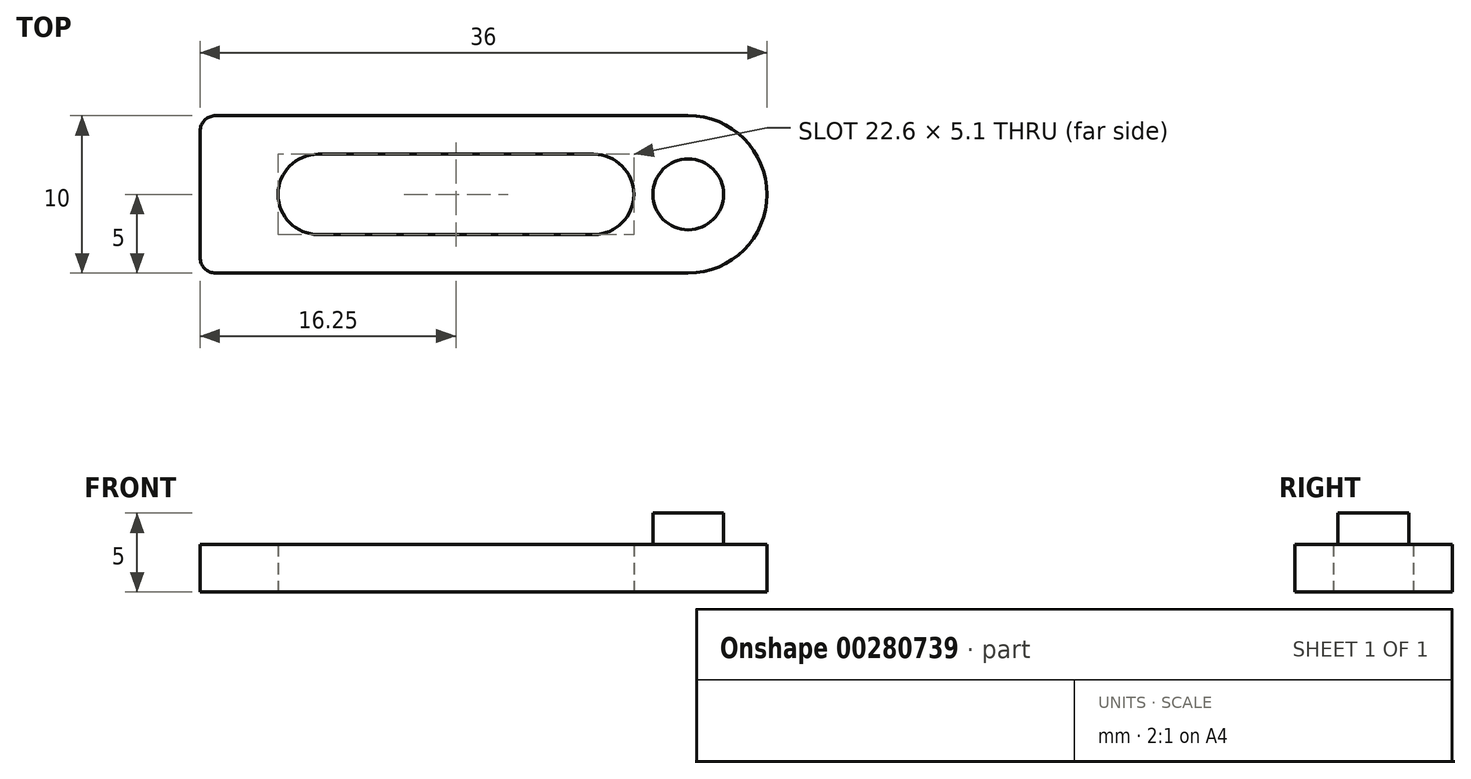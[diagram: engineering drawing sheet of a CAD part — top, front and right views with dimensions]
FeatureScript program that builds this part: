
annotation { "Feature Type Name" : "Feature", "Feature Type Description" : "" }
export const myFeature = defineFeature(function(context is Context, id is Id, definition is map)
    precondition{}
    {
        {
            var Q0;
            Q0=qCreatedBy(makeId("Top.planeOp"),FACE);
            var sketch = newSketch(context, id + "F0", { "sketchPlane" : qUnion([Q0])});
            skLineSegment(sketch, "E0.bottom", {"start": v(13.5, -5) * mm, "end": v(-16.5, -5) * mm});
            skLineSegment(sketch, "E0.top", {"start": v(13.5, 5) * mm, "end": v(-16.5, 5) * mm});
            skLineSegment(sketch, "E0.right", {"start": v(-17.5, -4) * mm, "end": v(-17.5, 4) * mm});
            skPoint(sketch, "E0.middle", {"position": v(0, 0) * mm});
            skLineSegment(sketch, "E1", {"start": v(-10, 0) * mm, "end": v(7.5, 0) * mm});
            skArc(sketch, "E2.0.startCap", {"start": v(-10, -2.55) * mm, "mid": v(-12.55, 0) * mm, "end": v(-10, 2.55) * mm});
            skArc(sketch, "E2.0.endCap", {"start": v(7.5, 2.55) * mm, "mid": v(10.05, 0) * mm, "end": v(7.5, -2.55) * mm});
            skLineSegment(sketch, "E2.0.left", {"start": v(-10, 2.55) * mm, "end": v(7.5, 2.55) * mm});
            skLineSegment(sketch, "E2.0.right", {"start": v(-10, -2.55) * mm, "end": v(7.5, -2.55) * mm});
            skPoint(sketch, "E3.visualSharp", {"position": v(-17.5, 5) * mm});
            skArc(sketch, "E3.filletArc", {"start": v(-16.5, 5) * mm, "mid": v(-17.2, 4.7) * mm, "end": v(-17.5, 4) * mm});
            skPoint(sketch, "E4.visualSharp", {"position": v(-17.5, -5) * mm});
            skArc(sketch, "E4.filletArc", {"start": v(-17.5, -4) * mm, "mid": v(-17.2, -4.7) * mm, "end": v(-16.5, -5) * mm});
            skPoint(sketch, "E5.visualSharp", {"position": v(17.5, -5) * mm});
            skPoint(sketch, "E6.visualSharp", {"position": v(17.5, 5) * mm});
            skCircle(sketch, "E7", {"center": v(13.5, 0) * mm, "radius": 2.25 * mm});
            skArc(sketch, "E8", {"start": v(13.5, -5) * mm, "mid": v(18.5, 0) * mm, "end": v(13.5, 5) * mm});
            skSolve(sketch);
        }
        {
            var Q0;
            Q0=makeQuery(id+"F0.imprint","IMPRINT",FACE,{"disambiguationData":[TD([[makeQuery(id+"F0.imprint","IMPRINT",EDGE,{"derivedFrom":sQuery(id+"F0.wireOp",EDGE,"E0.bottom")}),-1.0]])]});
            var Q1;
            Q1=makeQuery(id+"F0.imprint","IMPRINT",FACE,{"disambiguationData":[TD([[makeQuery(id+"F0.imprint","IMPRINT",EDGE,{"derivedFrom":sQuery(id+"F0.wireOp",EDGE,"E7")}),1.0]])]});
            extrude(context, id + "F1", {"entities" : qUnion([Q0, Q1]), "depth" : 3 * mm});
        }
        {
            var Q0;
            Q0=makeQuery(id+"F0.imprint","IMPRINT",FACE,{"disambiguationData":[TD([[makeQuery(id+"F0.imprint","IMPRINT",EDGE,{"derivedFrom":sQuery(id+"F0.wireOp",EDGE,"E7")}),1.0]])]});
            extrude(context, id + "F2", {"entities" : qUnion([Q0]), "operationType" : NewBodyOperationType.ADD, "depth" : 5 * mm});
        }
    });
